# Revit family: MarshallTufflex_ElectricalFittings_TrunkingDado_Mini_MMT1a
name_source: partatom
category: Generic Models
revit_build: Autodesk Revit 2016 (Build: 20150714_1515(x64)
units: mm (PartAtom-declared; Revit-internal decimal feet)

## family parameters
Can host rebar = No
Cut with Voids When Loaded = Yes
Host = Face
OmniClass Number = 23.80.30.17.14
OmniClass Title = Wireways
Part Type = Normal
Room Calculation Point = No
Round Connector Dimension = Use Diameter
Shared = Yes

## types (2) — shared parameters
Accessories = www.marshall-tufflex.com
Assembly Code = D5010
AssetType = Fixed
CEApproval = Yes
ClassificationName = Uniclass2015
ClassificationValue = Pr_65_70_11_61
Color = White (RAL9003)
Colour = White (RAL9003)
Compartments = No
Constituents = Mini Trunking
Default Elevation = 1200 mm
DocumentationCertificates = www.marshall-tufflex.com
DocumentationInstallationGuide = www.marshall-tufflex.com
DocumentationLiterature = www.marshall-tufflex.com
DocumentationMaintenance = www.marshall-tufflex.com
DocumentationTechnical = www.marshall-tufflex.com
DurationUnit = Years
EnclosureRating = IP4X
Features = Variety of sizes, self-fixing and punched options
Finish = Matt
Fittings = www.marshall-tufflex.com
IfcExportAs = IfcFlowSegment
IfcExportType = IfcCableSegmentType
Keynote = V90
LidConfiguration = Tamper Proof
LocationOfManufacturer = N 50°52'39" E 0°31'41"
Manufacturer = Marshall-Tufflex Ltd
ManufacturerName = Marshall-Tufflex Ltd
ManufacturerWebsite = www.marshall-tufflex.com
Material = PVCu
Model = Mini
ModelReference = Mini
NBSDescription = Proprietry Tunking
NBSReference = 90-55-10/390
NominalDepth = 16 mm  [stored 0.0524934 ft]
NominalHeight = 16 mm  [stored 0.0524934 ft]
NominalLength = 3000 mm  [stored 9.84252 ft]
O&Mmanual = www.marshall-tufflex.com
OverallHeight = 16 mm  [stored 0.0524934 ft]
OverallWidth = 16 mm  [stored 0.0524934 ft]
ProductLiterature = www.marshall-tufflex.com
ProductRange = Mini
ProductionYear = 2018
ReferenceStandard = BS EN 50085-1
ReferencedStandard = BS EN 50085-1
Shape = 16x16mm
Sub-Type = Dado
Type = Trunking
Type Comments = Dado Trunking Single Compartment With Cover
URL = www.marshall-tufflex.com
WarrantyDurationUnit = Years
_BSBibleVersion = 15
_CurrentRevision = 1
_DistributedBy = www.bimstore.co.uk
zero-valued in all types: AccessClearanceBottom, AccessClearanceFront, AccessClearanceLeft, AccessClearanceRear, AccessClearanceRight, AccessClearanceTop, Cost, EmbodiedCarbon, ExpectedLife, GreenGuideforSpecification, GrossWeight, ShippingWeight, WarrantyDurationLabor, WarrantyDurationParts, _BimSpecGuid

## per-type parameters (varying)
| type | BIMObjectName | Description | NBSObjectName | TypeName |
| MMT1 | MarshallTufflex_ElectricalFittings_TrunkingDado_Mini_MMT1 | Trunking Dado MT Mini MMT1 | MT MiniTrunkingMMT1 | Marshall Tufflex Electrical Fitting Trunking Dado Mini |
| MMT1SF | MarshallTufflex_ElectricalFittings_TrunkingDado_Mini_MMT1SF | Trunking Dado MT Mini MMT1SF | MT MiniTrunkingMMT1SF | Marshall Tufflex Electrical Fitting Trunking Dado Self Fixing Mini |

note: column(s) folded — value = type name in every type: ModelNumber, ProductModelNumber

note: [stored X ft] marks values corroborated as IEEE doubles in the binary element streams (Revit-internal decimal feet)

## geometry (parser evidence)
native form markers: Blend x2, Sweep x19
no freeform markers — native parametric forms only
